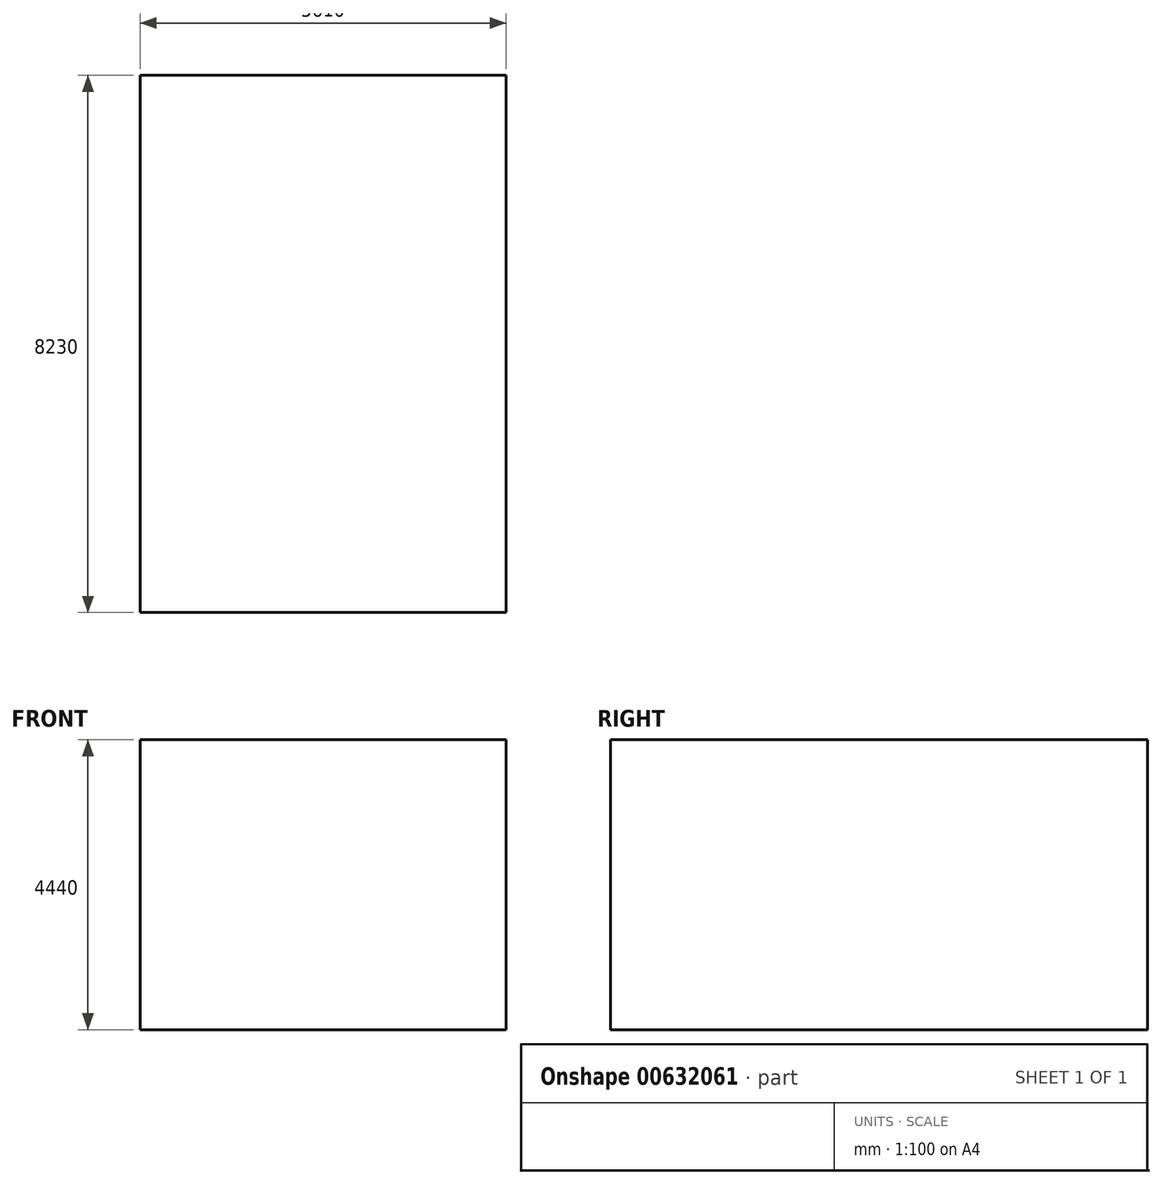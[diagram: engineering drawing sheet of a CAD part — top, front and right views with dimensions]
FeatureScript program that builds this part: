
annotation { "Feature Type Name" : "Feature", "Feature Type Description" : "" }
export const myFeature = defineFeature(function(context is Context, id is Id, definition is map)
    precondition{}
    {
        {
            var Q0;
            Q0=qCreatedBy(makeId("Front.planeOp"),FACE);
            var sketch = newSketch(context, id + "F0", { "sketchPlane" : qUnion([Q0])});
            skLineSegment(sketch, "E0.bottom", {"start": v(0, -2901.57) * mm, "end": v(5610, -2901.57) * mm});
            skLineSegment(sketch, "E0.top", {"start": v(0, 1538.43) * mm, "end": v(5610, 1538.43) * mm});
            skLineSegment(sketch, "E0.left", {"start": v(0, -2901.57) * mm, "end": v(0, 1538.43) * mm});
            skLineSegment(sketch, "E0.right", {"start": v(5610, -2901.57) * mm, "end": v(5610, 1538.43) * mm});
            skSolve(sketch);
        }
        {
            var Q0;
            Q0 = qSketchRegion(id + "F0", true);
            extrude(context, id + "F1", {"entities" : qUnion([Q0]), "depth" : 8230 * mm, "offsetDistance" : 25.4 * mm});
        }
    });
